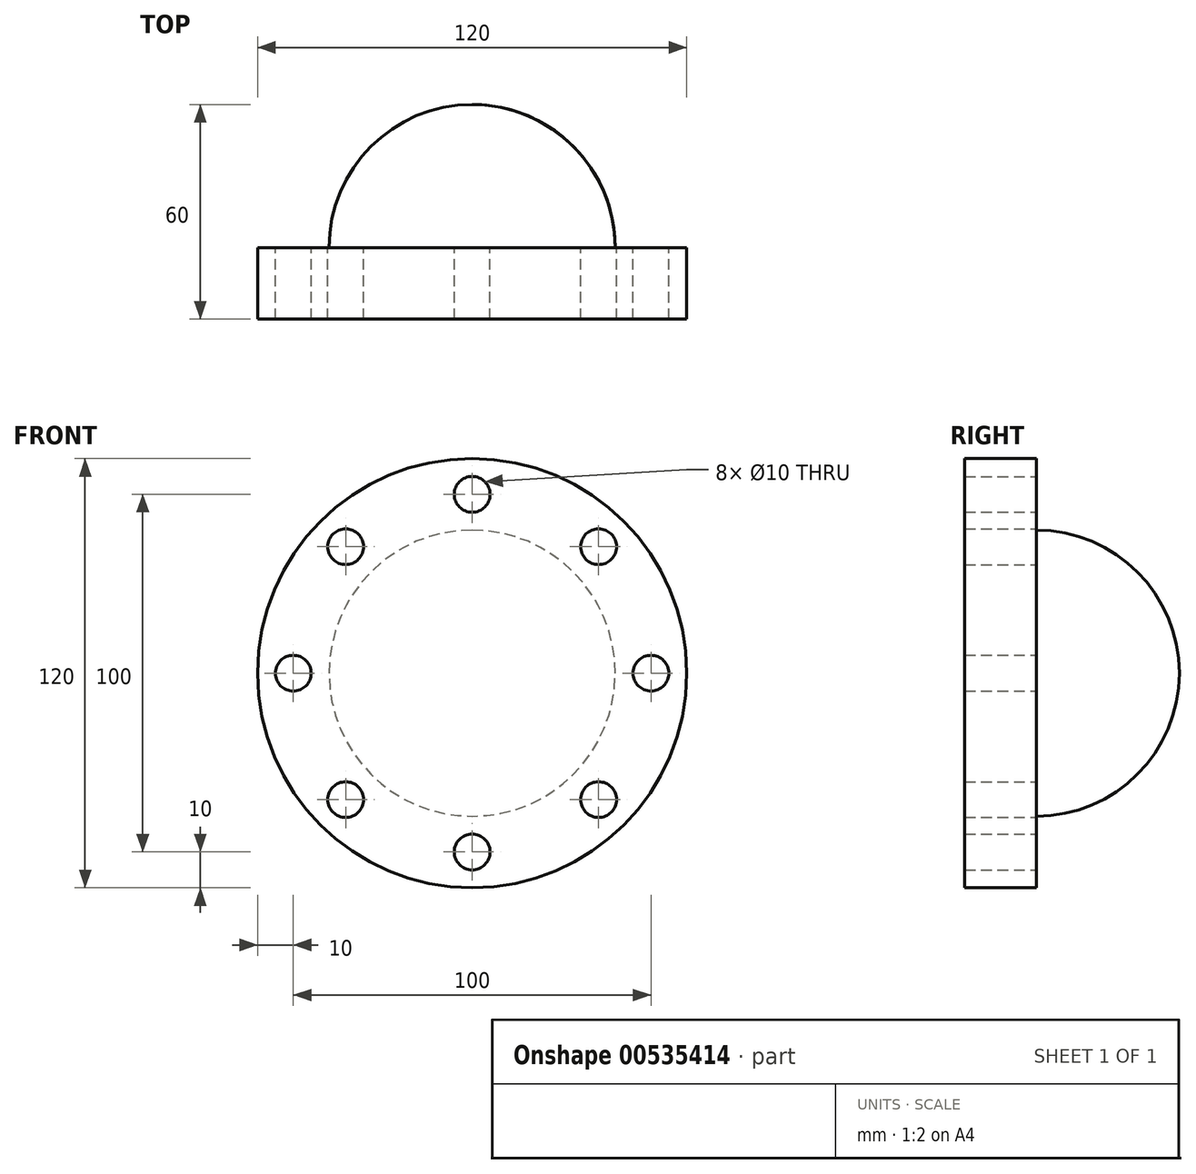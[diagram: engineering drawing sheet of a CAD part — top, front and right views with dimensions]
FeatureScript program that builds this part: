
annotation { "Feature Type Name" : "Feature", "Feature Type Description" : "" }
export const myFeature = defineFeature(function(context is Context, id is Id, definition is map)
    precondition{}
    {
        {
            var Q0;
            Q0=qCreatedBy(makeId("Front.planeOp"),FACE);
            var sketch = newSketch(context, id + "F0", { "sketchPlane" : qUnion([Q0])});
            skCircle(sketch, "E0", {"center": v(0, 0) * mm, "radius": 60 * mm});
            skCircle(sketch, "E1", {"center": v(0, 50) * mm, "radius": 5 * mm});
            skCircle(sketch, "E2.1.0", {"center": v(-35.36, 35.36) * mm, "radius": 5 * mm});
            skCircle(sketch, "E2.2.0", {"center": v(-50, 0) * mm, "radius": 5 * mm});
            skCircle(sketch, "E2.3.0", {"center": v(-35.36, -35.36) * mm, "radius": 5 * mm});
            skCircle(sketch, "E2.4.0", {"center": v(0, -50) * mm, "radius": 5 * mm});
            skCircle(sketch, "E2.5.0", {"center": v(35.36, -35.36) * mm, "radius": 5 * mm});
            skCircle(sketch, "E2.6.0", {"center": v(50, 0) * mm, "radius": 5 * mm});
            skCircle(sketch, "E2.7.0", {"center": v(35.36, 35.36) * mm, "radius": 5 * mm});
            skSolve(sketch);
        }
        {
            var Q0;
            Q0 = qSketchRegion(id + "F0", true);
            extrude(context, id + "F1", {"entities" : qUnion([Q0]), "depth" : 20 * mm, "offsetDistance" : 25 * mm});
        }
        {
            var Q0;
            Q0=qCreatedBy(makeId("Top.planeOp"),FACE);
            var sketch = newSketch(context, id + "F2", { "sketchPlane" : qUnion([Q0])});
            skArc(sketch, "E3", {"start": v(0, 40) * mm, "mid": v(-28.28, 28.28) * mm, "end": v(-40, 0) * mm});
            skLineSegment(sketch, "E4", {"start": v(0, 40) * mm, "end": v(0, 0) * mm});
            skLineSegment(sketch, "E5.0", {"start": v(0, 0) * mm, "end": v(-40, 0) * mm});
            skPoint(sketch, "E6.orphan", {"position": v(60, 0) * mm});
            skPoint(sketch, "E7.orphan", {"position": v(-60, 0) * mm});
            skSolve(sketch);
        }
        {
            var Q0;
            Q0 = qSketchRegion(id + "F2", true);
            var Q1;
            Q1=sQuery(id+"F2.wireOp",EDGE,"E4");
            revolve(context, id + "F3", {"operationType" : NewBodyOperationType.ADD, "entities" : qUnion([Q0]), "axis" : qUnion([Q1]), "revolveType" : RevolveType.FULL});
        }
    });
